# Revit family: PARLÉ TTM-X - Tabletop Microphone_rev1
name_source: partatom
category: Communication Devices
units: mm (PartAtom-declared; Revit-internal decimal feet)

## family parameters
Cut with Voids When Loaded = No
Host = Face
Maintain Annotation Orientation = No
Part Type = Normal
Room Calculation Point = Yes
Round Connector Dimension = Use Diameter
Shared = Yes

## types (4) — shared parameters
Connector = RJ-45 (cable length, 6.6 feet [2 meters])
Default Elevation = 4' - 0"
Depth = 0' - 0 11/16"
Dynamic Range = 90dB, A-Weighted
Excellent Acoustics Coverage = No
Fair Acoustics Coverage = No
Frequency Response = 150 Hz - 16 kHz: ± 3dB
Good Acoustics Coverage = Yes
Great Acoustics Coverage = No
Height = 0' - 4 5/16"
Manufacturer = Biamp Systems
Manufacturer URL = https://www.biamp.com
Maximum SPL (less than 1% THD) = 109dB
Microphone Technology = 16-Element Digital Array
Polar Pattern = Active Beamformed
Poor Acoustics Coverage = No
Product Documentation Link = https://downloads.biamp.com
Product Page URL = https://www.biamp.com
Room Acoustics Examples URL = https://support.biamp.com
SNR (at 1kHz, 94dBSPL A-Weighted) = > 74dB
Trim = Stainless Steel, Brushed
Weight Product = 0.5
Width = 0' - 4 5/16"

## per-type parameters (varying)
| type | Case Finish | Description | Mic Grille Finish | Model |
| PARLÉ™ TTM-X - Black | Black Finish | Low profile Beamtracking tabletop microphone. (Mic only. Requires TTM-xx Network Box. See TTM-xx Network Box for additional data and cost) | Black Grille - Fine | Parlé TTM-X - Black |
| PARLÉ™ TTM-X - White | Wear Resistant Textured White | Low profile Beamtracking tabletop microphone. (Mic only. Requires TTM-xx Network Box. See TTM-xx Network Box for additional data and cost) | Wear Resistant Textured White | Parlé TTM-X - White |
| PARLÉ™ TTM-XEX - White | Wear Resistant Textured White | Low profile Beamtracking tabletop microphone. (Expansion Mic only. (Must be used with TTM-X mic system. Cost is for expansion mic only) | Wear Resistant Textured White | Parlé TTM-XEX - White |
| PARLÉ™ TTM-XEX - Black | Black Finish | Low profile Beamtracking tabletop microphone. (Expansion Mic only. (Must be used with TTM-X mic system. Cost is for expansion mic only) | Black Grille - Fine | Parlé TTM-XEX - Black |

## geometry (parser evidence)
native form markers: Sweep x4
no freeform markers — native parametric forms only
